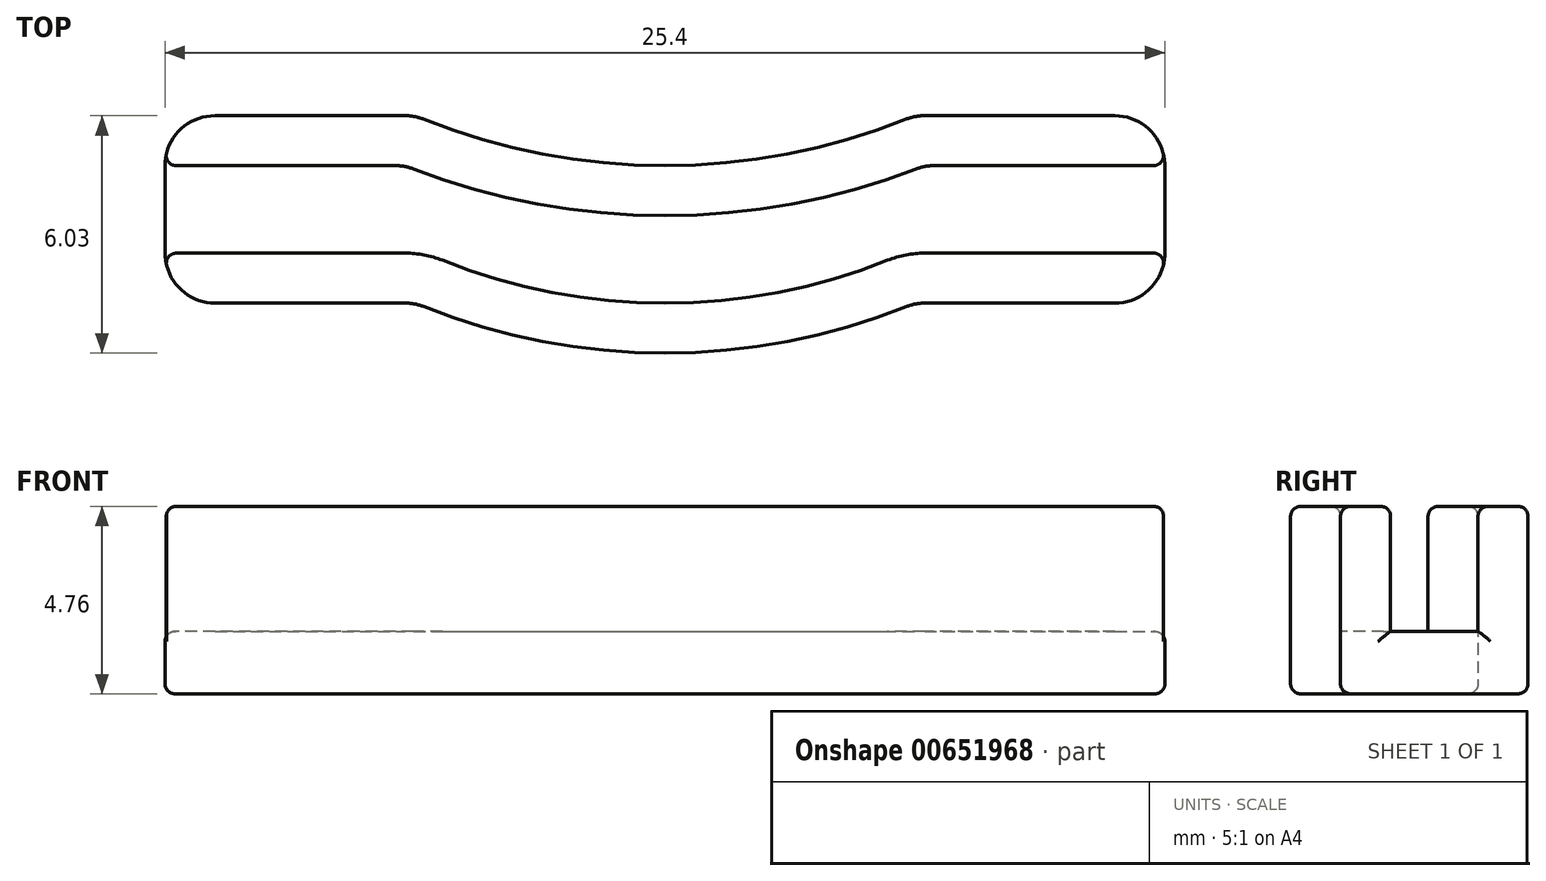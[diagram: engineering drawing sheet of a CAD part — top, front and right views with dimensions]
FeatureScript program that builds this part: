
annotation { "Feature Type Name" : "Feature", "Feature Type Description" : "" }
export const myFeature = defineFeature(function(context is Context, id is Id, definition is map)
    precondition{}
    {
        {
            var Q0;
            Q0=qCreatedBy(makeId("Top.planeOp"),FACE);
            var sketch = newSketch(context, id + "F0", { "sketchPlane" : qUnion([Q0])});
            skLineSegment(sketch, "E0", {"start": v(-11.43, 0) * mm, "end": v(-6.6, 0) * mm});
            skLineSegment(sketch, "E1", {"start": v(11.43, 0) * mm, "end": v(6.6, 0) * mm});
            skArc(sketch, "E2", {"start": v(-6.13, -0.1) * mm, "mid": v(0, -1.27) * mm, "end": v(6.13, -0.1) * mm});
            skPoint(sketch, "E2.third.point", {"position": v(0, -1.27) * mm});
            skLineSegment(sketch, "E3", {"start": v(-11.43, -4.76) * mm, "end": v(-6.6, -4.76) * mm});
            skLineSegment(sketch, "E4", {"start": v(11.43, -4.76) * mm, "end": v(6.6, -4.76) * mm});
            skArc(sketch, "E5", {"start": v(-6.12, -4.85) * mm, "mid": v(0, -6.03) * mm, "end": v(6.13, -4.85) * mm});
            skPoint(sketch, "E5.third.point", {"position": v(0, -6.03) * mm});
            skLineSegment(sketch, "E6", {"start": v(-12.7, -1.27) * mm, "end": v(-12.7, -3.5) * mm});
            skLineSegment(sketch, "E7", {"start": v(12.7, -3.5) * mm, "end": v(12.7, -1.27) * mm});
            skPoint(sketch, "E8.visualSharp", {"position": v(-12.7, 0) * mm});
            skArc(sketch, "E8.filletArc", {"start": v(-11.43, 0) * mm, "mid": v(-12.33, -0.37) * mm, "end": v(-12.7, -1.27) * mm});
            skPoint(sketch, "E9.visualSharp", {"position": v(-12.7, -4.76) * mm});
            skArc(sketch, "E9.filletArc", {"start": v(-12.7, -3.5) * mm, "mid": v(-12.32, -4.4) * mm, "end": v(-11.43, -4.76) * mm});
            skPoint(sketch, "E10.visualSharp", {"position": v(12.7, -4.76) * mm});
            skArc(sketch, "E10.filletArc", {"start": v(11.43, -4.76) * mm, "mid": v(12.33, -4.4) * mm, "end": v(12.7, -3.5) * mm});
            skPoint(sketch, "E11.visualSharp", {"position": v(12.7, 0) * mm});
            skArc(sketch, "E11.filletArc", {"start": v(12.7, -1.27) * mm, "mid": v(12.33, -0.37) * mm, "end": v(11.43, 0) * mm});
            skPoint(sketch, "E12.visualSharp", {"position": v(-6.35, 0) * mm});
            skArc(sketch, "E12.filletArc", {"start": v(-6.13, -0.1) * mm, "mid": v(-6.36, -0.02) * mm, "end": v(-6.6, 0) * mm});
            skPoint(sketch, "E13.visualSharp", {"position": v(6.35, 0) * mm});
            skArc(sketch, "E13.filletArc", {"start": v(6.6, 0) * mm, "mid": v(6.36, -0.02) * mm, "end": v(6.13, -0.1) * mm});
            skPoint(sketch, "E14.visualSharp", {"position": v(6.36, -4.76) * mm});
            skArc(sketch, "E14.filletArc", {"start": v(6.6, -4.76) * mm, "mid": v(6.36, -4.79) * mm, "end": v(6.13, -4.85) * mm});
            skPoint(sketch, "E15.visualSharp", {"position": v(-6.34, -4.76) * mm});
            skArc(sketch, "E15.filletArc", {"start": v(-6.12, -4.85) * mm, "mid": v(-6.35, -4.79) * mm, "end": v(-6.6, -4.76) * mm});
            skSolve(sketch);
        }
        {
            var Q0;
            Q0 = qSketchRegion(id + "F0", true);
            extrude(context, id + "F1", {"entities" : qUnion([Q0]), "depth" : 1.59 * mm, "offsetDistance" : 25.4 * mm});
        }
        {
            var Q0;
            Q0=makeQuery(id+"F1.opExtrude","CAP_FACE",FACE,{"disambiguationData":[OSD([sQuery(id+"F0.wireOp",EDGE,"E0"),sQuery(id+"F0.wireOp",EDGE,"E1"),sQuery(id+"F0.wireOp",EDGE,"E2"),sQuery(id+"F0.wireOp",EDGE,"E3"),sQuery(id+"F0.wireOp",EDGE,"E4"),sQuery(id+"F0.wireOp",EDGE,"E5"),sQuery(id+"F0.wireOp",EDGE,"E6"),sQuery(id+"F0.wireOp",EDGE,"E7"),sQuery(id+"F0.wireOp",EDGE,"E8.filletArc"),sQuery(id+"F0.wireOp",EDGE,"E9.filletArc"),sQuery(id+"F0.wireOp",EDGE,"E10.filletArc"),sQuery(id+"F0.wireOp",EDGE,"E11.filletArc"),sQuery(id+"F0.wireOp",EDGE,"E12.filletArc"),sQuery(id+"F0.wireOp",EDGE,"E13.filletArc"),sQuery(id+"F0.wireOp",EDGE,"E14.filletArc"),sQuery(id+"F0.wireOp",EDGE,"E15.filletArc")])],"isStart":false});
            var sketch = newSketch(context, id + "F2", { "sketchPlane" : qUnion([Q0])});
            skArc(sketch, "E16.0", {"start": v(5.66, -3.67) * mm, "mid": v(6.12, -3.54) * mm, "end": v(6.6, -3.5) * mm});
            skArc(sketch, "E16.1", {"start": v(-5.65, -3.67) * mm, "mid": v(0, -4.76) * mm, "end": v(5.66, -3.67) * mm});
            skArc(sketch, "E16.2", {"start": v(-6.6, -3.5) * mm, "mid": v(-6.11, -3.54) * mm, "end": v(-5.65, -3.67) * mm});
            skLineSegment(sketch, "E16.3", {"start": v(-11.43, -3.5) * mm, "end": v(-6.6, -3.5) * mm});
            skLineSegment(sketch, "E16.4", {"start": v(-11.43, -3.5) * mm, "end": v(-11.43, -3.5) * mm});
            skLineSegment(sketch, "E16.5", {"start": v(11.43, -1.27) * mm, "end": v(6.84, -1.27) * mm});
            skLineSegment(sketch, "E16.6", {"start": v(11.43, -1.27) * mm, "end": v(11.43, -1.27) * mm});
            skLineSegment(sketch, "E16.8", {"start": v(11.43, -3.5) * mm, "end": v(11.43, -3.5) * mm});
            skArc(sketch, "E16.10", {"start": v(6.38, -1.35) * mm, "mid": v(0, -2.54) * mm, "end": v(-6.38, -1.35) * mm});
            skLineSegment(sketch, "E16.12", {"start": v(-6.84, -1.27) * mm, "end": v(-11.43, -1.27) * mm});
            skLineSegment(sketch, "E16.13", {"start": v(-11.43, -1.27) * mm, "end": v(-11.43, -1.27) * mm});
            skLineSegment(sketch, "E16.14", {"start": v(6.6, -3.5) * mm, "end": v(11.43, -3.5) * mm});
            skLineSegment(sketch, "E17.0", {"start": v(-11.43, 0) * mm, "end": v(-6.6, 0) * mm});
            skArc(sketch, "E17.1", {"start": v(-6.13, -0.1) * mm, "mid": v(-6.36, -0.02) * mm, "end": v(-6.6, 0) * mm});
            skArc(sketch, "E17.2", {"start": v(-6.13, -0.1) * mm, "mid": v(0, -1.27) * mm, "end": v(6.13, -0.1) * mm});
            skArc(sketch, "E17.3", {"start": v(-6.12, -4.85) * mm, "mid": v(0, -6.03) * mm, "end": v(6.13, -4.85) * mm});
            skArc(sketch, "E17.4", {"start": v(-6.12, -4.85) * mm, "mid": v(-6.35, -4.79) * mm, "end": v(-6.6, -4.76) * mm});
            skLineSegment(sketch, "E17.5", {"start": v(-11.43, -4.76) * mm, "end": v(-6.6, -4.76) * mm});
            skArc(sketch, "E17.6", {"start": v(-12.7, -3.5) * mm, "mid": v(-12.32, -4.4) * mm, "end": v(-11.43, -4.76) * mm});
            skArc(sketch, "E17.8", {"start": v(-11.43, 0) * mm, "mid": v(-12.33, -0.37) * mm, "end": v(-12.7, -1.27) * mm});
            skArc(sketch, "E17.9", {"start": v(6.6, -4.76) * mm, "mid": v(6.36, -4.79) * mm, "end": v(6.13, -4.85) * mm});
            skLineSegment(sketch, "E17.10", {"start": v(11.43, -4.76) * mm, "end": v(6.6, -4.76) * mm});
            skArc(sketch, "E17.12", {"start": v(11.43, -4.76) * mm, "mid": v(12.33, -4.4) * mm, "end": v(12.7, -3.5) * mm});
            skArc(sketch, "E17.13", {"start": v(12.7, -1.27) * mm, "mid": v(12.33, -0.37) * mm, "end": v(11.43, 0) * mm});
            skLineSegment(sketch, "E17.14", {"start": v(11.43, 0) * mm, "end": v(6.6, 0) * mm});
            skArc(sketch, "E17.15", {"start": v(6.6, 0) * mm, "mid": v(6.36, -0.02) * mm, "end": v(6.13, -0.1) * mm});
            skLineSegment(sketch, "E18", {"start": v(-11.43, -1.27) * mm, "end": v(-12.7, -1.27) * mm});
            skLineSegment(sketch, "E19", {"start": v(-11.43, -3.5) * mm, "end": v(-12.7, -3.5) * mm});
            skLineSegment(sketch, "E20", {"start": v(11.43, -3.5) * mm, "end": v(12.7, -3.5) * mm});
            skLineSegment(sketch, "E21", {"start": v(11.43, -1.27) * mm, "end": v(12.7, -1.27) * mm});
            skArc(sketch, "E22.filletArc", {"start": v(-6.38, -1.35) * mm, "mid": v(-6.6, -1.3) * mm, "end": v(-6.84, -1.27) * mm});
            skArc(sketch, "E23.filletArc", {"start": v(6.84, -1.27) * mm, "mid": v(6.6, -1.3) * mm, "end": v(6.38, -1.35) * mm});
            skSolve(sketch);
        }
        {
            var Q0;
            Q0 = qSketchRegion(id + "F2", true);
            extrude(context, id + "F3", {"entities" : qUnion([Q0]), "operationType" : NewBodyOperationType.ADD, "depth" : 3.17 * mm, "offsetDistance" : 25.4 * mm});
        }
        {
            var Q0;
            Q0=makeQuery(id+"F1.opExtrude","CAP_EDGE",EDGE,{"disambiguationData":[OSD([sQuery(id+"F0.wireOp",EDGE,"E7")])],"isStart":false});
            var Q1;
            Q1=makeQuery(id+"F3.opExtrude","SWEPT_EDGE",EDGE,{"disambiguationData":[OSD([sQuery(id+"F0.wireOp",EDGE,"E7"),sQuery(id+"F2.wireOp",EDGE,"E17.13"),sQuery(id+"F2.wireOp",EDGE,"E21")])]});
            var Q2;
            Q2=makeQuery(id+"F3.opExtrude","SWEPT_EDGE",EDGE,{"disambiguationData":[OSD([sQuery(id+"F0.wireOp",EDGE,"E7"),sQuery(id+"F2.wireOp",EDGE,"E17.12"),sQuery(id+"F2.wireOp",EDGE,"E20")])]});
            var Q3;
            Q3=makeQuery(id+"F3.opExtrude","SWEPT_EDGE",EDGE,{"disambiguationData":[OSD([sQuery(id+"F2.wireOp",EDGE,"E16.5"),sQuery(id+"F2.wireOp",EDGE,"E16.10")])]});
            var Q4;
            Q4=makeQuery(id+"F1.opExtrude","CAP_EDGE",EDGE,{"disambiguationData":[OSD([sQuery(id+"F0.wireOp",EDGE,"E7")])],"isStart":true});
            var Q5;
            Q5=makeQuery(id+"F3.opExtrude","SWEPT_EDGE",EDGE,{"disambiguationData":[OSD([sQuery(id+"F0.wireOp",EDGE,"E6"),sQuery(id+"F2.wireOp",EDGE,"E17.8"),sQuery(id+"F2.wireOp",EDGE,"E18")])]});
            var Q6;
            Q6=makeQuery(id+"F3.opExtrude","SWEPT_EDGE",EDGE,{"disambiguationData":[OSD([sQuery(id+"F0.wireOp",EDGE,"E6"),sQuery(id+"F2.wireOp",EDGE,"E17.6"),sQuery(id+"F2.wireOp",EDGE,"E19")])]});
            var Q7;
            Q7=makeQuery(id+"F3.opExtrude","CAP_EDGE",EDGE,{"disambiguationData":[OSD([sQuery(id+"F2.wireOp",EDGE,"E16.1")])],"isStart":false});
            var Q8;
            Q8=makeQuery(id+"F3.opExtrude","CAP_EDGE",EDGE,{"disambiguationData":[OSD([sQuery(id+"F2.wireOp",EDGE,"E17.5")])],"isStart":false});
            var Q9;
            Q9=makeQuery(id+"F3.opExtrude","CAP_EDGE",EDGE,{"disambiguationData":[OSD([sQuery(id+"F2.wireOp",EDGE,"E17.0")])],"isStart":false});
            var Q10;
            Q10=makeQuery(id+"F3.opExtrude","CAP_EDGE",EDGE,{"disambiguationData":[OSD([sQuery(id+"F2.wireOp",EDGE,"E16.10")])],"isStart":false});
            var Q11;
            Q11=makeQuery(id+"F3.opExtrude","CAP_EDGE",EDGE,{"disambiguationData":[OSD([sQuery(id+"F2.wireOp",EDGE,"E16.12")])],"isStart":false});
            var Q12;
            Q12=makeQuery(id+"F3.opExtrude","CAP_EDGE",EDGE,{"disambiguationData":[OSD([sQuery(id+"F2.wireOp",EDGE,"E17.8")])],"isStart":false});
            var Q13;
            Q13=makeQuery(id+"F3.opExtrude","CAP_EDGE",EDGE,{"disambiguationData":[OSD([sQuery(id+"F2.wireOp",EDGE,"E18")])],"isStart":false});
            var Q14;
            Q14=makeQuery(id+"F1.opExtrude","CAP_EDGE",EDGE,{"disambiguationData":[OSD([sQuery(id+"F0.wireOp",EDGE,"E6")])],"isStart":false});
            fillet(context, id + "F4", {"entities" : qUnion([Q0, Q1, Q2, Q3, Q4, Q5, Q6, Q7, Q8, Q9, Q10, Q11, Q12, Q13, Q14]), "radius" : 0.25 * mm, "tangentPropagation" : true, "allowEdgeOverflow" : false});
        }
    });
